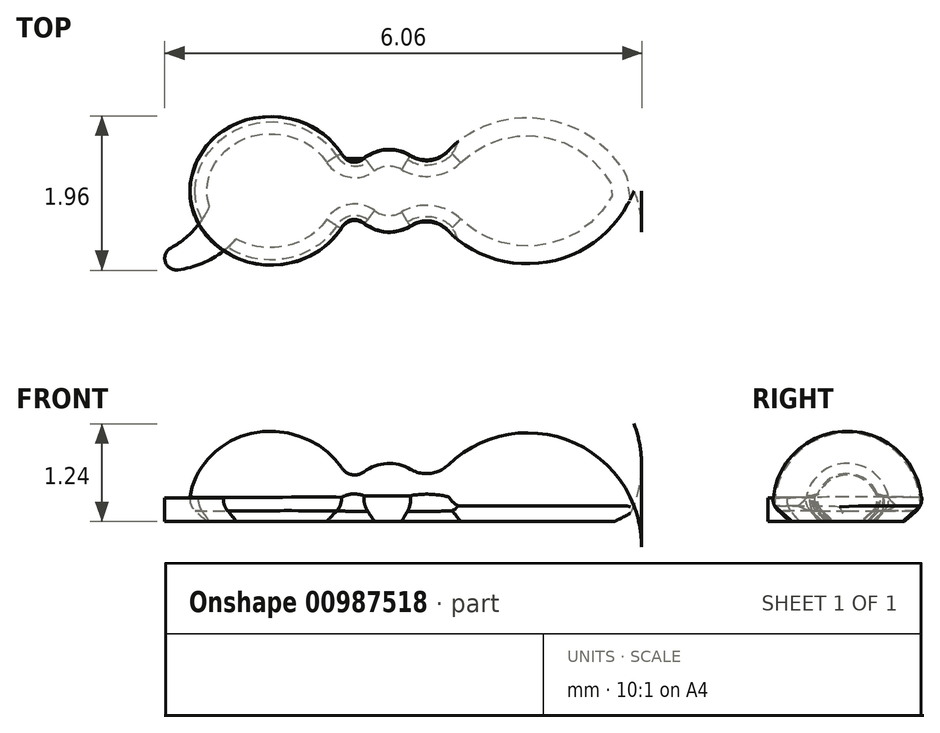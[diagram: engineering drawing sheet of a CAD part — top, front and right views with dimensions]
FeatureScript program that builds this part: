
annotation { "Feature Type Name" : "Feature", "Feature Type Description" : "" }
export const myFeature = defineFeature(function(context is Context, id is Id, definition is map)
    precondition{}
    {
        {
            var Q0;
            Q0=qCreatedBy(makeId("Top.planeOp"),FACE);
            var sketch = newSketch(context, id + "F0", { "sketchPlane" : qUnion([Q0])});
            skLineSegment(sketch, "E0.bottom", {"start": v(0.5, -0.4) * mm, "end": v(-0.5, -0.4) * mm, "construction": true});
            skLineSegment(sketch, "E0.top", {"start": v(0.5, 0.4) * mm, "end": v(-0.5, 0.4) * mm, "construction": true});
            skLineSegment(sketch, "E0.left", {"start": v(0.5, -0.4) * mm, "end": v(0.5, 0.4) * mm, "construction": true});
            skLineSegment(sketch, "E0.right", {"start": v(-0.5, -0.4) * mm, "end": v(-0.5, 0.4) * mm, "construction": true});
            skPoint(sketch, "E0.middle", {"position": v(0, 0) * mm});
            skLineSegment(sketch, "E1.bottom", {"start": v(0.5, -0.4) * mm, "end": v(3, -0.4) * mm, "construction": true});
            skLineSegment(sketch, "E1.top", {"start": v(0.5, 0.4) * mm, "end": v(3, 0.4) * mm, "construction": true});
            skLineSegment(sketch, "E1.left", {"start": v(0.5, -0.4) * mm, "end": v(0.5, 0.4) * mm});
            skLineSegment(sketch, "E1.right", {"start": v(3, -0.4) * mm, "end": v(3, 0.4) * mm, "construction": true});
            skLineSegment(sketch, "E2.bottom", {"start": v(-0.5, -0.4) * mm, "end": v(-2.5, -0.4) * mm, "construction": true});
            skLineSegment(sketch, "E2.top", {"start": v(-0.5, 0.4) * mm, "end": v(-2.5, 0.4) * mm, "construction": true});
            skLineSegment(sketch, "E2.right", {"start": v(-2.5, -0.4) * mm, "end": v(-2.5, 0.4) * mm, "construction": true});
            skPoint(sketch, "E3.centerSnap0", {"position": v(-1.5, 0.4) * mm});
            skPoint(sketch, "E3.centerSnap1", {"position": v(-0.5, 0) * mm});
            skArc(sketch, "E4", {"start": v(3.1, 0) * mm, "mid": v(1.87, 0.92) * mm, "end": v(0.5, 0.2) * mm});
            skPoint(sketch, "E4.endSnap0", {"position": v(0.5, 0) * mm});
            skPoint(sketch, "E5.orphan", {"position": v(2.12, 1.92) * mm});
            skPoint(sketch, "E6.orphan", {"position": v(2.12, -1.92) * mm});
            skLineSegment(sketch, "E7", {"start": v(-2.54, 0) * mm, "end": v(3.1, 0) * mm});
            skPoint(sketch, "E8.trimOffspring.end.orphan", {"position": v(0.5, -0.2) * mm});
            skArc(sketch, "E9.trimOffspring", {"start": v(0.5, 0.2) * mm, "mid": v(0.01, 0.54) * mm, "end": v(-0.49, 0.22) * mm});
            skEllipticalArc(sketch, "E10.trimOffspring", {});
            const initialGuessF0  = {"E10.trimOffspring": [-0.0015, 0, 1, 0, 0.0010376893851192885, 0.00095, 0.23134508231783438, 3.141592653589793]};
            skSetInitialGuess(sketch, initialGuessF0);
            skSolve(sketch);
        }
        {
            var Q0;
            Q0 = qSketchRegion(id + "F0", true);
            var Q1;
            Q1=sQuery(id+"F0.wireOp",EDGE,"E7");
            revolve(context, id + "F1", {"surfaceOperationType" : NewSurfaceOperationType.NEW, "entities" : qUnion([Q0]), "axis" : qUnion([Q1]), "revolveType" : RevolveType.FULL});
        }
        {
            var Q0;
            Q0=makeQuery(id+"F1.opRevolve","SWEPT_EDGE",EDGE,{"disambiguationData":[OSD([sQuery(id+"F0.wireOp",EDGE,"E1.left"),sQuery(id+"F0.wireOp",EDGE,"E4"),sQuery(id+"F0.wireOp",EDGE,"E9.trimOffspring")])]});
            fillet(context, id + "F2", {"entities" : qUnion([Q0]), "tangentPropagation" : true, "radius" : .4 * mm, "defaultsChanged" : true, "vertexSettings" : [], "allowEdgeOverflow" : false});
        }
        {
            var Q0;
            Q0=makeQuery(id+"F1.opRevolve","SWEPT_EDGE",EDGE,{"disambiguationData":[OSD([sQuery(id+"F0.wireOp",EDGE,"E9.trimOffspring"),sQuery(id+"F0.wireOp",EDGE,"E10.trimOffspring")])]});
            fillet(context, id + "F3", {"entities" : qUnion([Q0]), "tangentPropagation" : true, "radius" : .2 * mm, "defaultsChanged" : true, "vertexSettings" : [], "allowEdgeOverflow" : false});
        }
        {
            var Q0;
            Q0=qCreatedBy(makeId("Right.planeOp"),FACE);
            var sketch = newSketch(context, id + "F4", { "sketchPlane" : qUnion([Q0])});
            skLineSegment(sketch, "E11.bottom", {"start": v(-3, -0.2) * mm, "end": v(3, -0.2) * mm});
            skLineSegment(sketch, "E11.top", {"start": v(-3, -2.2) * mm, "end": v(3, -2.2) * mm});
            skLineSegment(sketch, "E11.left", {"start": v(-3, -0.2) * mm, "end": v(-3, -2.2) * mm});
            skLineSegment(sketch, "E11.right", {"start": v(3, -0.2) * mm, "end": v(3, -2.2) * mm});
            skPoint(sketch, "E11.middle", {"position": v(0, -1.2) * mm});
            skSolve(sketch);
        }
        {
            var Q0;
            Q0 = qSketchRegion(id + "F4", true);
            extrude(context, id + "F5", {"entities" : qUnion([Q0]), "operationType" : NewBodyOperationType.REMOVE, "depth" : 25 * mm, "offsetDistance" : 25 * mm, "hasSecondDirection" : true, "secondDirectionOppositeDirection" : true, "secondDirectionDepth" : 25 * mm});
        }
        {
            var Q0;
            Q0=makeQuery(id+"F5.boolean.opBoolean","INTERSECT",EDGE,{"derivedFrom":[makeQuery(id+"F1.opRevolve","SWEPT_FACE",FACE,{"disambiguationData":[OSD([sQuery(id+"F0.wireOp",EDGE,"E10.trimOffspring")])]}),makeQuery(id+"F5.opExtrude","SWEPT_FACE",FACE,{"disambiguationData":[OSD([sQuery(id+"F4.wireOp",EDGE,"E11.bottom")])]})]});
            var Q1;
            Q1=makeQuery(id+"F5.boolean.opBoolean","INTERSECT",EDGE,{"disambiguationData":[OD(1.0)],"derivedFrom":[makeQuery(id+"F1.opRevolve","SWEPT_FACE",FACE,{"disambiguationData":[OSD([sQuery(id+"F0.wireOp",EDGE,"E9.trimOffspring")])]}),makeQuery(id+"F5.opExtrude","SWEPT_FACE",FACE,{"disambiguationData":[OSD([sQuery(id+"F4.wireOp",EDGE,"E11.bottom")])]})]});
            var Q2;
            Q2=makeQuery(id+"F5.boolean.opBoolean","INTERSECT",EDGE,{"disambiguationData":[OD(1.0)],"derivedFrom":[makeQuery(id+"F3.opFillet","BLEND_FACE",FACE,{"disambiguationData":[OSD([sQuery(id+"F0.wireOp",EDGE,"E9.trimOffspring"),sQuery(id+"F0.wireOp",EDGE,"E10.trimOffspring")])]}),makeQuery(id+"F5.opExtrude","SWEPT_FACE",FACE,{"disambiguationData":[OSD([sQuery(id+"F4.wireOp",EDGE,"E11.bottom")])]})]});
            var Q3;
            Q3=makeQuery(id+"F5.boolean.opBoolean","INTERSECT",EDGE,{"disambiguationData":[OD(1.0)],"derivedFrom":[makeQuery(id+"F2.opFillet","BLEND_FACE",FACE,{"disambiguationData":[OSD([sQuery(id+"F0.wireOp",EDGE,"E1.left"),sQuery(id+"F0.wireOp",EDGE,"E4"),sQuery(id+"F0.wireOp",EDGE,"E9.trimOffspring")])]}),makeQuery(id+"F5.opExtrude","SWEPT_FACE",FACE,{"disambiguationData":[OSD([sQuery(id+"F4.wireOp",EDGE,"E11.bottom")])]})]});
            var Q4;
            Q4=makeQuery(id+"F5.boolean.opBoolean","INTERSECT",EDGE,{"derivedFrom":[makeQuery(id+"F1.opRevolve","SWEPT_FACE",FACE,{"disambiguationData":[OSD([sQuery(id+"F0.wireOp",EDGE,"E4")])]}),makeQuery(id+"F5.opExtrude","SWEPT_FACE",FACE,{"disambiguationData":[OSD([sQuery(id+"F4.wireOp",EDGE,"E11.bottom")])]})]});
            var Q5;
            Q5=makeQuery(id+"F5.boolean.opBoolean","INTERSECT",EDGE,{"disambiguationData":[OD(0.0)],"derivedFrom":[makeQuery(id+"F1.opRevolve","SWEPT_FACE",FACE,{"disambiguationData":[OSD([sQuery(id+"F0.wireOp",EDGE,"E9.trimOffspring")])]}),makeQuery(id+"F5.opExtrude","SWEPT_FACE",FACE,{"disambiguationData":[OSD([sQuery(id+"F4.wireOp",EDGE,"E11.bottom")])]})]});
            var Q6;
            Q6=makeQuery(id+"F5.boolean.opBoolean","INTERSECT",EDGE,{"disambiguationData":[OD(0.0)],"derivedFrom":[makeQuery(id+"F2.opFillet","BLEND_FACE",FACE,{"disambiguationData":[OSD([sQuery(id+"F0.wireOp",EDGE,"E1.left"),sQuery(id+"F0.wireOp",EDGE,"E4"),sQuery(id+"F0.wireOp",EDGE,"E9.trimOffspring")])]}),makeQuery(id+"F5.opExtrude","SWEPT_FACE",FACE,{"disambiguationData":[OSD([sQuery(id+"F4.wireOp",EDGE,"E11.bottom")])]})]});
            var Q7;
            Q7=makeQuery(id+"F5.boolean.opBoolean","INTERSECT",EDGE,{"disambiguationData":[OD(0.0)],"derivedFrom":[makeQuery(id+"F3.opFillet","BLEND_FACE",FACE,{"disambiguationData":[OSD([sQuery(id+"F0.wireOp",EDGE,"E9.trimOffspring"),sQuery(id+"F0.wireOp",EDGE,"E10.trimOffspring")])]}),makeQuery(id+"F5.opExtrude","SWEPT_FACE",FACE,{"disambiguationData":[OSD([sQuery(id+"F4.wireOp",EDGE,"E11.bottom")])]})]});
            chamfer(context, id + "F6", {"entities" : qUnion([Q0, Q1, Q2, Q3, Q4, Q5, Q6, Q7]), "width" : .2 * mm, "tangentPropagation" : true});
        }
        {
            var Q0;
            {var subQ0=makeQuery(id+"F1.opRevolve","SWEPT_FACE",FACE,{"disambiguationData":[OSD([sQuery(id+"F0.wireOp",EDGE,"E10.trimOffspring")])]});Q0=makeQuery(id+"F6.opChamfer","BLEND_EDGE",EDGE,{"blendedFrom":[makeQuery(id+"F5.boolean.opBoolean","INTERSECT",EDGE,{"derivedFrom":[subQ0,makeQuery(id+"F5.opExtrude","SWEPT_FACE",FACE,{"disambiguationData":[OSD([sQuery(id+"F4.wireOp",EDGE,"E11.bottom")])]})]}),subQ0],"blendedInto":[subQ0]});}
            var Q1;
            {var subQ0=makeQuery(id+"F3.opFillet","BLEND_FACE",FACE,{"disambiguationData":[OSD([sQuery(id+"F0.wireOp",EDGE,"E9.trimOffspring"),sQuery(id+"F0.wireOp",EDGE,"E10.trimOffspring")])]});Q1=makeQuery(id+"F6.opChamfer","BLEND_EDGE",EDGE,{"blendedFrom":[makeQuery(id+"F5.boolean.opBoolean","INTERSECT",EDGE,{"disambiguationData":[OD(1.0)],"derivedFrom":[subQ0,makeQuery(id+"F5.opExtrude","SWEPT_FACE",FACE,{"disambiguationData":[OSD([sQuery(id+"F4.wireOp",EDGE,"E11.bottom")])]})]}),subQ0],"blendedInto":[subQ0]});}
            var Q2;
            {var subQ0=makeQuery(id+"F1.opRevolve","SWEPT_FACE",FACE,{"disambiguationData":[OSD([sQuery(id+"F0.wireOp",EDGE,"E9.trimOffspring")])]});Q2=makeQuery(id+"F6.opChamfer","BLEND_EDGE",EDGE,{"blendedFrom":[makeQuery(id+"F5.boolean.opBoolean","INTERSECT",EDGE,{"disambiguationData":[OD(1.0)],"derivedFrom":[subQ0,makeQuery(id+"F5.opExtrude","SWEPT_FACE",FACE,{"disambiguationData":[OSD([sQuery(id+"F4.wireOp",EDGE,"E11.bottom")])]})]}),subQ0],"blendedInto":[subQ0]});}
            var Q3;
            {var subQ0=makeQuery(id+"F2.opFillet","BLEND_FACE",FACE,{"disambiguationData":[OSD([sQuery(id+"F0.wireOp",EDGE,"E1.left"),sQuery(id+"F0.wireOp",EDGE,"E4"),sQuery(id+"F0.wireOp",EDGE,"E9.trimOffspring")])]});Q3=makeQuery(id+"F6.opChamfer","BLEND_EDGE",EDGE,{"blendedFrom":[makeQuery(id+"F5.boolean.opBoolean","INTERSECT",EDGE,{"disambiguationData":[OD(1.0)],"derivedFrom":[subQ0,makeQuery(id+"F5.opExtrude","SWEPT_FACE",FACE,{"disambiguationData":[OSD([sQuery(id+"F4.wireOp",EDGE,"E11.bottom")])]})]}),subQ0],"blendedInto":[subQ0]});}
            var Q4;
            {var subQ0=makeQuery(id+"F3.opFillet","BLEND_FACE",FACE,{"disambiguationData":[OSD([sQuery(id+"F0.wireOp",EDGE,"E9.trimOffspring"),sQuery(id+"F0.wireOp",EDGE,"E10.trimOffspring")])]});Q4=makeQuery(id+"F6.opChamfer","BLEND_EDGE",EDGE,{"blendedFrom":[makeQuery(id+"F5.boolean.opBoolean","INTERSECT",EDGE,{"disambiguationData":[OD(0.0)],"derivedFrom":[subQ0,makeQuery(id+"F5.opExtrude","SWEPT_FACE",FACE,{"disambiguationData":[OSD([sQuery(id+"F4.wireOp",EDGE,"E11.bottom")])]})]}),subQ0],"blendedInto":[subQ0]});}
            var Q5;
            {var subQ0=makeQuery(id+"F1.opRevolve","SWEPT_FACE",FACE,{"disambiguationData":[OSD([sQuery(id+"F0.wireOp",EDGE,"E9.trimOffspring")])]});Q5=makeQuery(id+"F6.opChamfer","BLEND_EDGE",EDGE,{"blendedFrom":[makeQuery(id+"F5.boolean.opBoolean","INTERSECT",EDGE,{"disambiguationData":[OD(0.0)],"derivedFrom":[subQ0,makeQuery(id+"F5.opExtrude","SWEPT_FACE",FACE,{"disambiguationData":[OSD([sQuery(id+"F4.wireOp",EDGE,"E11.bottom")])]})]}),subQ0],"blendedInto":[subQ0]});}
            var Q6;
            {var subQ0=makeQuery(id+"F2.opFillet","BLEND_FACE",FACE,{"disambiguationData":[OSD([sQuery(id+"F0.wireOp",EDGE,"E1.left"),sQuery(id+"F0.wireOp",EDGE,"E4"),sQuery(id+"F0.wireOp",EDGE,"E9.trimOffspring")])]});Q6=makeQuery(id+"F6.opChamfer","BLEND_EDGE",EDGE,{"blendedFrom":[makeQuery(id+"F5.boolean.opBoolean","INTERSECT",EDGE,{"disambiguationData":[OD(0.0)],"derivedFrom":[subQ0,makeQuery(id+"F5.opExtrude","SWEPT_FACE",FACE,{"disambiguationData":[OSD([sQuery(id+"F4.wireOp",EDGE,"E11.bottom")])]})]}),subQ0],"blendedInto":[subQ0]});}
            fillet(context, id + "F7", {"entities" : qUnion([Q0, Q1, Q2, Q3, Q4, Q5, Q6]), "tangentPropagation" : true, "radius" : .2 * mm, "defaultsChanged" : true, "vertexSettings" : [], "allowEdgeOverflow" : false});
        }
        {
            var Q0;
            Q0=makeQuery(id+"F5.boolean.opBoolean","COPY",FACE,{"derivedFrom":makeQuery(id+"F5.opExtrude","SWEPT_FACE",FACE,{"disambiguationData":[OSD([sQuery(id+"F4.wireOp",EDGE,"E11.bottom")])]})});
            var sketch = newSketch(context, id + "F8", { "sketchPlane" : qUnion([Q0])});
            skLineSegment(sketch, "E12.bottom", {"start": v(-0.8, -1.5) * mm, "end": v(-1.2, -1.5) * mm});
            skLineSegment(sketch, "E12.top", {"start": v(-0.8, 1.5) * mm, "end": v(-1.2, 1.5) * mm});
            skLineSegment(sketch, "E12.left", {"start": v(-0.8, -1.5) * mm, "end": v(-0.8, 1.5) * mm});
            skLineSegment(sketch, "E12.right", {"start": v(-1.2, -1.5) * mm, "end": v(-1.2, 1.5) * mm});
            skPoint(sketch, "E12.middle", {"position": v(-1, 0) * mm});
            skLineSegment(sketch, "E13.bottom", {"start": v(0.2, -1.5) * mm, "end": v(-0.2, -1.5) * mm});
            skLineSegment(sketch, "E13.top", {"start": v(0.2, 1.5) * mm, "end": v(-0.2, 1.5) * mm});
            skLineSegment(sketch, "E13.left", {"start": v(0.2, -1.5) * mm, "end": v(0.2, 1.5) * mm});
            skLineSegment(sketch, "E13.right", {"start": v(-0.2, -1.5) * mm, "end": v(-0.2, 1.5) * mm});
            skPoint(sketch, "E13.middle", {"position": v(0, 0) * mm});
            skLineSegment(sketch, "E14.bottom", {"start": v(1.4, -1.5) * mm, "end": v(1, -1.5) * mm});
            skLineSegment(sketch, "E14.top", {"start": v(1.4, 1.5) * mm, "end": v(1, 1.5) * mm});
            skLineSegment(sketch, "E14.left", {"start": v(1.4, -1.5) * mm, "end": v(1.4, 1.5) * mm});
            skLineSegment(sketch, "E14.right", {"start": v(1, -1.5) * mm, "end": v(1, 1.5) * mm});
            skPoint(sketch, "E14.middle", {"position": v(1.2, 0) * mm});
            skSolve(sketch);
        }
        {
            var Q0;
            Q0=makeQuery(id+"Fp6tdSng1BP8C0A_1.boolean.opBoolean","MERGE",FACE,{"derivedFrom":[makeQuery(id+"F5.boolean.opBoolean","COPY",FACE,{"derivedFrom":makeQuery(id+"F5.opExtrude","SWEPT_FACE",FACE,{"disambiguationData":[OSD([sQuery(id+"F4.wireOp",EDGE,"E11.bottom")])]})}),makeQuery(id+"Fp6tdSng1BP8C0A_1.opExtrude","CAP_FACE",FACE,{"disambiguationData":[OSD([sQuery(id+"F8.wireOp",EDGE,"E12.bottom"),sQuery(id+"F8.wireOp",EDGE,"E12.top"),sQuery(id+"F8.wireOp",EDGE,"E12.left"),sQuery(id+"F8.wireOp",EDGE,"E12.right")])],"isStart":true}),makeQuery(id+"Fp6tdSng1BP8C0A_1.opExtrude","CAP_FACE",FACE,{"disambiguationData":[OSD([sQuery(id+"F8.wireOp",EDGE,"E13.bottom"),sQuery(id+"F8.wireOp",EDGE,"E13.top"),sQuery(id+"F8.wireOp",EDGE,"E13.left"),sQuery(id+"F8.wireOp",EDGE,"E13.right")])],"isStart":true}),makeQuery(id+"Fp6tdSng1BP8C0A_1.opExtrude","CAP_FACE",FACE,{"disambiguationData":[OSD([sQuery(id+"F8.wireOp",EDGE,"E14.bottom"),sQuery(id+"F8.wireOp",EDGE,"E14.top"),sQuery(id+"F8.wireOp",EDGE,"E14.left"),sQuery(id+"F8.wireOp",EDGE,"E14.right")])],"isStart":true})]});
            var sketch = newSketch(context, id + "F9", { "sketchPlane" : qUnion([Q0])});
            skArc(sketch, "E15", {"start": v(-1.92, 0.59) * mm, "mid": v(-2.65, 1) * mm, "end": v(-3.47, 0.84) * mm});
            skArc(sketch, "E16", {"start": v(-2.27, 0.15) * mm, "mid": v(-2.74, 0.7) * mm, "end": v(-3.47, 0.84) * mm});
            skArc(sketch, "E17.MirrorCS", {"start": v(-2.27, -0.15) * mm, "mid": v(-2.74, -0.7) * mm, "end": v(-3.47, -0.84) * mm});
            skArc(sketch, "E18.MirrorCS", {"start": v(-1.92, -0.59) * mm, "mid": v(-2.65, -1) * mm, "end": v(-3.47, -0.84) * mm});
            skSolve(sketch);
        }
        {
            var Q0;
            {var subQ0=sQuery(id+"F9.wireOp",EDGE,"E15");Q0=makeQuery(id+"F9.imprint","IMPRINT",FACE,{"disambiguationData":[TD([[makeQuery(id+"F9.imprint","IMPRINT",EDGE,{"derivedFrom":subQ0}),1.0]])]});}
            var Q1;
            {var subQ0=sQuery(id+"F9.wireOp",EDGE,"E17.MirrorCS");Q1=makeQuery(id+"F9.imprint","IMPRINT",FACE,{"disambiguationData":[TD([[makeQuery(id+"F9.imprint","IMPRINT",EDGE,{"derivedFrom":subQ0}),1.0]])]});}
            extrude(context, id + "F10", {"entities" : qUnion([Q0, Q1]), "operationType" : NewBodyOperationType.ADD, "oppositeDirection" : true, "depth" : .3 * mm, "offsetDistance" : 25 * mm});
        }
        {
            var Q0;
            Q0=makeQuery(id+"F10.opExtrude","SWEPT_EDGE",EDGE,{"disambiguationData":[OSD([sQuery(id+"F9.wireOp",EDGE,"E17.MirrorCS"),sQuery(id+"F9.wireOp",EDGE,"E18.MirrorCS")])]});
            var Q1;
            Q1=makeQuery(id+"F10.opExtrude","SWEPT_EDGE",EDGE,{"disambiguationData":[OSD([sQuery(id+"F9.wireOp",EDGE,"E15"),sQuery(id+"F9.wireOp",EDGE,"E16")])]});
            fillet(context, id + "F11", {"entities" : qUnion([Q0, Q1]), "tangentPropagation" : true, "radius" : .15 * mm, "defaultsChanged" : true, "vertexSettings" : [], "allowEdgeOverflow" : false});
        }
    });
